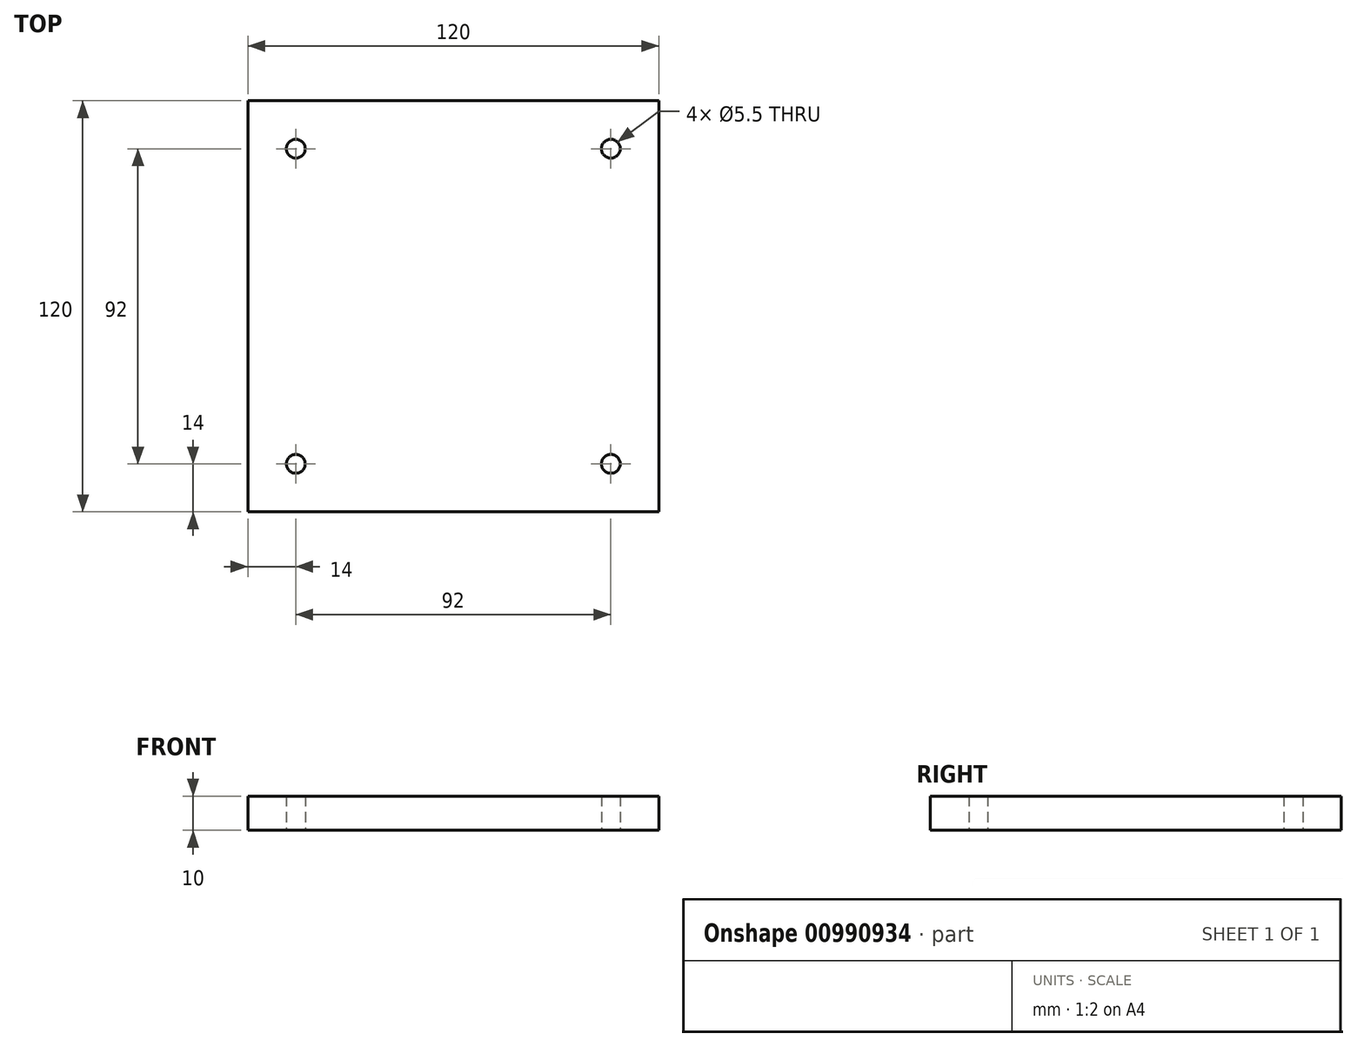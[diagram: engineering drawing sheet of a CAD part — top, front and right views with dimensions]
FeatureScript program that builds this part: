
annotation { "Feature Type Name" : "Feature", "Feature Type Description" : "" }
export const myFeature = defineFeature(function(context is Context, id is Id, definition is map)
    precondition{}
    {
        {
            var Q0;
            Q0=qCreatedBy(makeId("Top.planeOp"),FACE);
            var sketch = newSketch(context, id + "F0", { "sketchPlane" : qUnion([Q0])});
            skLineSegment(sketch, "E0.bottom", {"start": v(60, -60) * mm, "end": v(-60, -60) * mm});
            skLineSegment(sketch, "E0.top", {"start": v(60, 60) * mm, "end": v(-60, 60) * mm});
            skLineSegment(sketch, "E0.left", {"start": v(60, -60) * mm, "end": v(60, 60) * mm});
            skLineSegment(sketch, "E0.right", {"start": v(-60, -60) * mm, "end": v(-60, 60) * mm});
            skPoint(sketch, "E0.middle", {"position": v(0, 0) * mm});
            skCircle(sketch, "E1", {"center": v(-46, 46) * mm, "radius": 2.75 * mm});
            skCircle(sketch, "E2.MirrorC", {"center": v(46, 46) * mm, "radius": 2.75 * mm});
            skCircle(sketch, "E3.MirrorC", {"center": v(-46, -46) * mm, "radius": 2.75 * mm});
            skCircle(sketch, "E4.MirrorC", {"center": v(46, -46) * mm, "radius": 2.75 * mm});
            skSolve(sketch);
        }
        {
            var Q0;
            Q0 = qSketchRegion(id + "F0", true);
            extrude(context, id + "F1", {"entities" : qUnion([Q0]), "depth" : 10 * mm, "offsetDistance" : 25 * mm});
        }
    });
